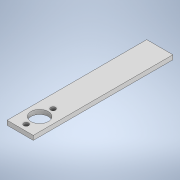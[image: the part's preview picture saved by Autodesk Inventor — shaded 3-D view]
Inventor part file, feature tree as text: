
AUTODESK INVENTOR PART (.ipt)
format: ipt  version: 2020 (Build 240168000, 168)  size: 107,008 bytes
history: native  units: in
note: dims shown in document units (in); Inventor stores cm internally (conversion verified against a paired STEP export)
features: extrude x2, sketch x2
ambient origin geometry x8: Origin, YZ Plane, XZ Plane, XY Plane, X Axis, Y Axis, Z Axis, Center Point
bodies: Solid1 (feature_tree)
feature tree (4):
  extrude  "Extrusion1"  Depth=4.0in
  extrude  "Extrusion2"  Depth=0.125in
  sketch  "Sketch1"  dims[d0=0.75in d1=4.0in]
  sketch  "Sketch2"  dims[d2=0.125in d3=0.0in d4=0.77in d5=0.141in d6=0.141in d7=0.5in d8=0.125in d9=0.0in]
